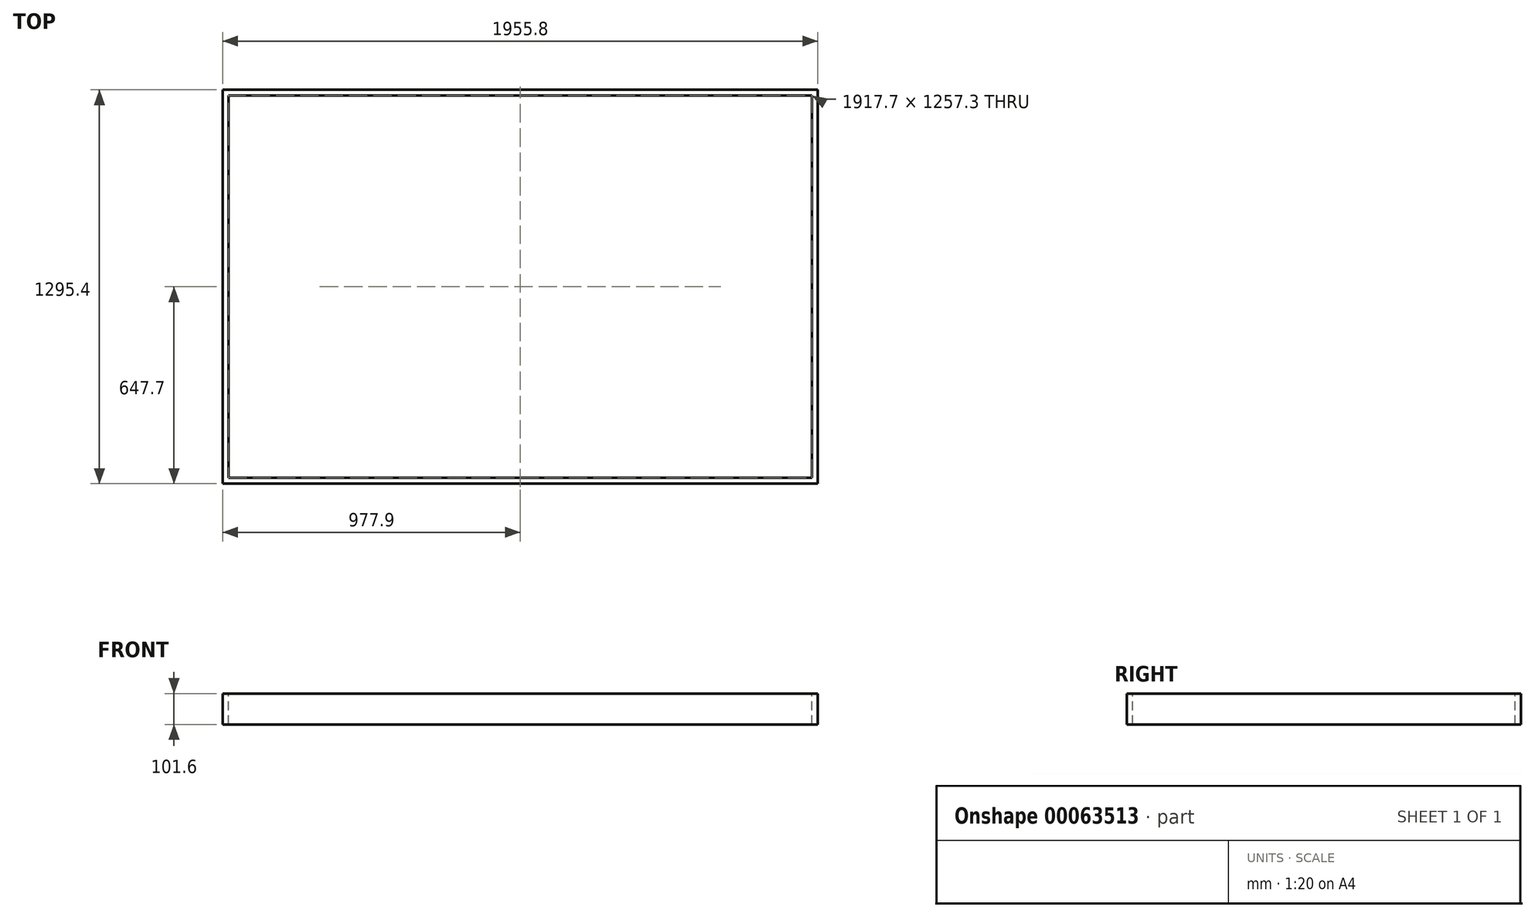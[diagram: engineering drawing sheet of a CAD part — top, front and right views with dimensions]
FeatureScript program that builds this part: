
annotation { "Feature Type Name" : "Feature", "Feature Type Description" : "" }
export const myFeature = defineFeature(function(context is Context, id is Id, definition is map)
    precondition{}
    {
        {
            var Q0;
            Q0=qCreatedBy(makeId("Top.planeOp"),FACE);
            var sketch = newSketch(context, id + "F0", { "sketchPlane" : qUnion([Q0])});
            skLineSegment(sketch, "E0.rect.bottom", {"start": v(-977.9, 647.7) * mm, "end": v(977.9, 647.7) * mm});
            skLineSegment(sketch, "E0.rect.top", {"start": v(-977.9, -647.7) * mm, "end": v(977.9, -647.7) * mm});
            skLineSegment(sketch, "E0.rect.left", {"start": v(-977.9, 647.7) * mm, "end": v(-977.9, -647.7) * mm});
            skLineSegment(sketch, "E0.rect.right", {"start": v(977.9, 647.7) * mm, "end": v(977.9, -647.7) * mm});
            skPoint(sketch, "E0.rect.middle", {"position": v(0, 0) * mm});
            skSolve(sketch);
        }
        {
            var Q0;
            Q0=makeQuery(id+"F0.imprint","IMPRINT",FACE,{"disambiguationData":[TD([[makeQuery(id+"F0.imprint","IMPRINT",EDGE,{"derivedFrom":sQuery(id+"F0.wireOp",EDGE,"E0.rect.bottom")}),-1.0]])]});
            extrude(context, id + "F1", {"entities" : qUnion([Q0]), "depth" : 101.6 * mm});
        }
        {
            var Q0;
            Q0=makeQuery(id+"F1.opExtrude","CAP_FACE",FACE,{"disambiguationData":[OSD([sQuery(id+"F0.wireOp",EDGE,"E0.rect.bottom"),sQuery(id+"F0.wireOp",EDGE,"E0.rect.top"),sQuery(id+"F0.wireOp",EDGE,"E0.rect.left"),sQuery(id+"F0.wireOp",EDGE,"E0.rect.right")])],"isStart":false});
            var sketch = newSketch(context, id + "F2", { "sketchPlane" : qUnion([Q0])});
            skLineSegment(sketch, "E1.rect.bottom", {"start": v(-958.85, 628.65) * mm, "end": v(958.85, 628.65) * mm});
            skLineSegment(sketch, "E1.rect.top", {"start": v(-958.85, -628.65) * mm, "end": v(958.85, -628.65) * mm});
            skLineSegment(sketch, "E1.rect.left", {"start": v(-958.85, 628.65) * mm, "end": v(-958.85, -628.65) * mm});
            skLineSegment(sketch, "E1.rect.right", {"start": v(958.85, 628.65) * mm, "end": v(958.85, -628.65) * mm});
            skPoint(sketch, "E1.rect.middle", {"position": v(0, 0) * mm});
            skSolve(sketch);
        }
        {
            var Q0;
            Q0=makeQuery(id+"F2.imprint","IMPRINT",FACE,{"disambiguationData":[TD([[makeQuery(id+"F2.imprint","IMPRINT",EDGE,{"derivedFrom":sQuery(id+"F2.wireOp",EDGE,"E1.rect.bottom")}),-1.0]])]});
            extrude(context, id + "F3", {"entities" : qUnion([Q0]), "operationType" : NewBodyOperationType.REMOVE, "endBound" : BoundingType.THROUGH_ALL, "oppositeDirection" : true, "depth" : 25.4 * mm});
        }
    });
